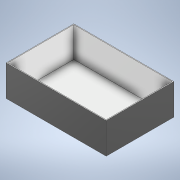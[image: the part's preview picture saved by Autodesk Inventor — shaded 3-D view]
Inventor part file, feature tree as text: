
AUTODESK INVENTOR PART (.ipt)
format: ipt  version: 2021 (Build 250183000, 183)  size: 110,080 bytes
history: native  units: mm
features: extrude x2, sketch x1
ambient origin geometry x8: Origin, YZ Plane, XZ Plane, XY Plane, X Axis, Y Axis, Z Axis, Center Point
bodies: Solid1 (feature_tree)
feature tree (3):
  sketch  "Sketch1"  dims[d0=425.45mm d1=285.5mm d2=3.175mm d3=3.175mm d4=0.0mm d5=130.175mm d6=0.0mm]
  extrude  "Extrusion1"  Depth=285.5mm
  extrude  "Extrusion2"  Depth=3.175mm
